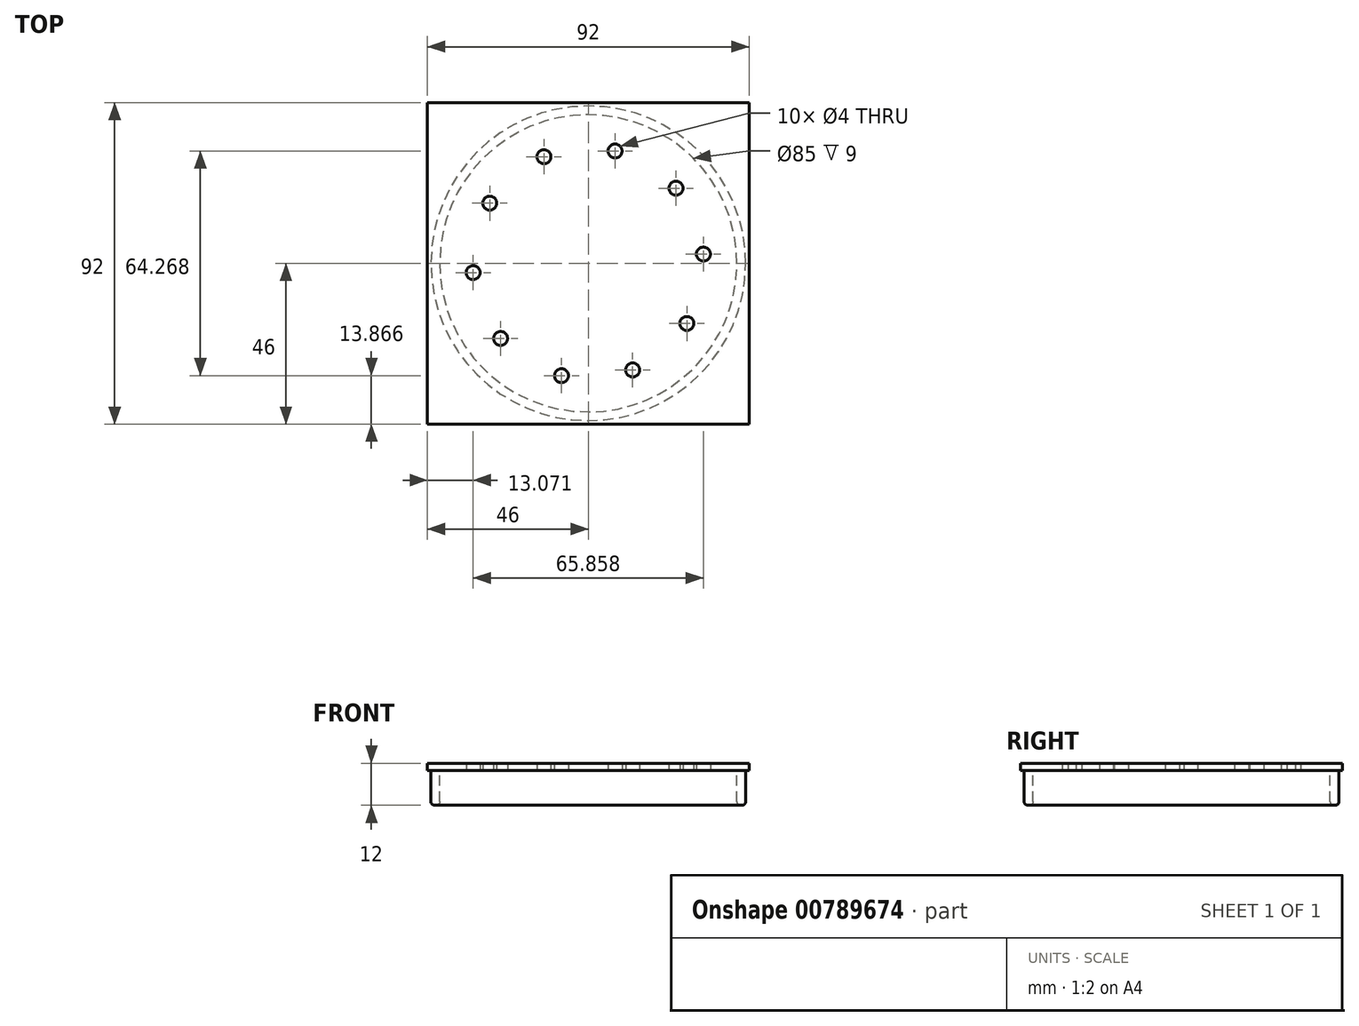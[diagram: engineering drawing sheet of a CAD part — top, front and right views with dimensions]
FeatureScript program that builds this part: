
annotation { "Feature Type Name" : "Feature", "Feature Type Description" : "" }
export const myFeature = defineFeature(function(context is Context, id is Id, definition is map)
    precondition{}
    {
        {
            var Q0;
            Q0=qCreatedBy(makeId("Top.planeOp"),FACE);
            var sketch = newSketch(context, id + "F0", { "sketchPlane" : qUnion([Q0])});
            skCircle(sketch, "E0", {"center": v(0, 0) * mm, "radius": 45 * mm});
            skSolve(sketch);
        }
        {
            var Q0;
            Q0 = qSketchRegion(id + "F0", true);
            var Q1;
            Q1=makeQuery(id+"F0.imprint","IMPRINT",FACE,{"disambiguationData":[TD([[makeQuery(id+"F0.imprint","IMPRINT",EDGE,{"derivedFrom":sQuery(id+"F0.wireOp",EDGE,"E0")}),1.0]])]});
            extrude(context, id + "F1", {"entities" : qUnion([Q0, Q1]), "oppositeDirection" : true, "depth" : 10 * mm, "offsetDistance" : 25 * mm});
        }
        {
            var Q0;
            Q0=makeQuery(id+"F1.opExtrude","CAP_FACE",FACE,{"disambiguationData":[OSD([sQuery(id+"F0.wireOp",EDGE,"E0")])],"isStart":true});
            var Q1;
            Q1=makeQuery(id+"F1.opExtrude","CAP_FACE",FACE,{"disambiguationData":[OSD([sQuery(id+"F0.wireOp",EDGE,"E0")])],"isStart":false});
            shell(context, id + "F2", {"entities" : qUnion([Q0, Q1]), "thickness" : 2.5 * mm});
        }
        {
            var Q0;
            Q0=makeQuery(id+"F1.opExtrude","CAP_FACE",FACE,{"disambiguationData":[OSD([sQuery(id+"F0.wireOp",EDGE,"E0")])],"isStart":true});
            var sketch = newSketch(context, id + "F3", { "sketchPlane" : qUnion([Q0])});
            skLineSegment(sketch, "E1.bottom", {"start": v(-46, 46) * mm, "end": v(46, 46) * mm});
            skLineSegment(sketch, "E1.top", {"start": v(-46, -46) * mm, "end": v(46, -46) * mm});
            skLineSegment(sketch, "E1.left", {"start": v(-46, 46) * mm, "end": v(-46, -46) * mm});
            skLineSegment(sketch, "E1.right", {"start": v(46, 46) * mm, "end": v(46, -46) * mm});
            skPoint(sketch, "E1.middle", {"position": v(0, 0) * mm});
            skSolve(sketch);
        }
        {
            var Q0;
            Q0 = qSketchRegion(id + "F3", true);
            extrude(context, id + "F4", {"entities" : qUnion([Q0]), "operationType" : NewBodyOperationType.ADD, "depth" : 2 * mm, "offsetDistance" : 25 * mm});
        }
        {
            var Q0;
            Q0=makeQuery(id+"F4.boolean.opBoolean","SPLIT",FACE,{"disambiguationData":[TD([makeQuery(id+"F2.opShell","OFFSET_FACE",FACE,{"disambiguationData":[OSD([sQuery(id+"F0.wireOp",EDGE,"E0")])]})])],"derivedFrom":makeQuery(id+"F4.opExtrude","CAP_FACE",FACE,{"disambiguationData":[OSD([sQuery(id+"F3.wireOp",EDGE,"E1.bottom"),sQuery(id+"F3.wireOp",EDGE,"E1.top"),sQuery(id+"F3.wireOp",EDGE,"E1.left"),sQuery(id+"F3.wireOp",EDGE,"E1.right")])],"isStart":true})});
            var sketch = newSketch(context, id + "F5", { "sketchPlane" : qUnion([Q0])});
            skCircle(sketch, "E2", {"center": v(12.69, 30.5) * mm, "radius": 2 * mm});
            skCircle(sketch, "E3.1.0", {"center": v(-7.66, 32.13) * mm, "radius": 2 * mm});
            skCircle(sketch, "E3.2.0", {"center": v(-25.09, 21.5) * mm, "radius": 2 * mm});
            skCircle(sketch, "E3.3.0", {"center": v(-32.93, 2.64) * mm, "radius": 2 * mm});
            skCircle(sketch, "E3.4.0", {"center": v(-28.2, -17.22) * mm, "radius": 2 * mm});
            skCircle(sketch, "E3.5.0", {"center": v(-12.69, -30.5) * mm, "radius": 2 * mm});
            skCircle(sketch, "E3.6.0", {"center": v(7.66, -32.13) * mm, "radius": 2 * mm});
            skCircle(sketch, "E3.7.0", {"center": v(25.09, -21.5) * mm, "radius": 2 * mm});
            skCircle(sketch, "E3.8.0", {"center": v(32.93, -2.64) * mm, "radius": 2 * mm});
            skCircle(sketch, "E3.9.0", {"center": v(28.2, 17.22) * mm, "radius": 2 * mm});
            skPoint(sketch, "E3.center", {"position": v(0, 0) * mm});
            skSolve(sketch);
        }
        {
            var Q0;
            Q0=makeQuery(id+"F5.imprint","IMPRINT",FACE,{"disambiguationData":[TD([[makeQuery(id+"F5.imprint","IMPRINT",EDGE,{"derivedFrom":sQuery(id+"F5.wireOp",EDGE,"E3.1.0")}),1.0]])]});
            var Q1;
            Q1=makeQuery(id+"F5.imprint","IMPRINT",FACE,{"disambiguationData":[TD([[makeQuery(id+"F5.imprint","IMPRINT",EDGE,{"derivedFrom":sQuery(id+"F5.wireOp",EDGE,"E2")}),1.0]])]});
            var Q2;
            Q2=makeQuery(id+"F5.imprint","IMPRINT",FACE,{"disambiguationData":[TD([[makeQuery(id+"F5.imprint","IMPRINT",EDGE,{"derivedFrom":sQuery(id+"F5.wireOp",EDGE,"E3.9.0")}),1.0]])]});
            var Q3;
            Q3=makeQuery(id+"F5.imprint","IMPRINT",FACE,{"disambiguationData":[TD([[makeQuery(id+"F5.imprint","IMPRINT",EDGE,{"derivedFrom":sQuery(id+"F5.wireOp",EDGE,"E3.8.0")}),1.0]])]});
            var Q4;
            Q4=makeQuery(id+"F5.imprint","IMPRINT",FACE,{"disambiguationData":[TD([[makeQuery(id+"F5.imprint","IMPRINT",EDGE,{"derivedFrom":sQuery(id+"F5.wireOp",EDGE,"E3.7.0")}),1.0]])]});
            var Q5;
            Q5=makeQuery(id+"F5.imprint","IMPRINT",FACE,{"disambiguationData":[TD([[makeQuery(id+"F5.imprint","IMPRINT",EDGE,{"derivedFrom":sQuery(id+"F5.wireOp",EDGE,"E3.2.0")}),1.0]])]});
            var Q6;
            Q6=makeQuery(id+"F5.imprint","IMPRINT",FACE,{"disambiguationData":[TD([[makeQuery(id+"F5.imprint","IMPRINT",EDGE,{"derivedFrom":sQuery(id+"F5.wireOp",EDGE,"E3.3.0")}),1.0]])]});
            var Q7;
            Q7=makeQuery(id+"F5.imprint","IMPRINT",FACE,{"disambiguationData":[TD([[makeQuery(id+"F5.imprint","IMPRINT",EDGE,{"derivedFrom":sQuery(id+"F5.wireOp",EDGE,"E3.4.0")}),1.0]])]});
            var Q8;
            Q8=makeQuery(id+"F5.imprint","IMPRINT",FACE,{"disambiguationData":[TD([[makeQuery(id+"F5.imprint","IMPRINT",EDGE,{"derivedFrom":sQuery(id+"F5.wireOp",EDGE,"E3.5.0")}),1.0]])]});
            var Q9;
            Q9=makeQuery(id+"F5.imprint","IMPRINT",FACE,{"disambiguationData":[TD([[makeQuery(id+"F5.imprint","IMPRINT",EDGE,{"derivedFrom":sQuery(id+"F5.wireOp",EDGE,"E3.6.0")}),1.0]])]});
            extrude(context, id + "F6", {"entities" : qUnion([Q0, Q1, Q2, Q3, Q4, Q5, Q6, Q7, Q8, Q9]), "operationType" : NewBodyOperationType.REMOVE, "oppositeDirection" : true, "depth" : 6 * mm, "offsetDistance" : 25 * mm});
        }
        {
            var Q0;
            Q0=makeQuery(id+"F1.opExtrude","CAP_EDGE",EDGE,{"disambiguationData":[OSD([sQuery(id+"F0.wireOp",EDGE,"E0")])],"isStart":false});
            var Q1;
            Q1=makeQuery(id+"F1.opExtrude","CAP_FACE",FACE,{"disambiguationData":[OSD([sQuery(id+"F0.wireOp",EDGE,"E0")])],"isStart":false});
            fillet(context, id + "F7", {"entities" : qUnion([Q0, Q1]), "radius" : 1 * mm, "tangentPropagation" : true, "allowEdgeOverflow" : false});
        }
    });
